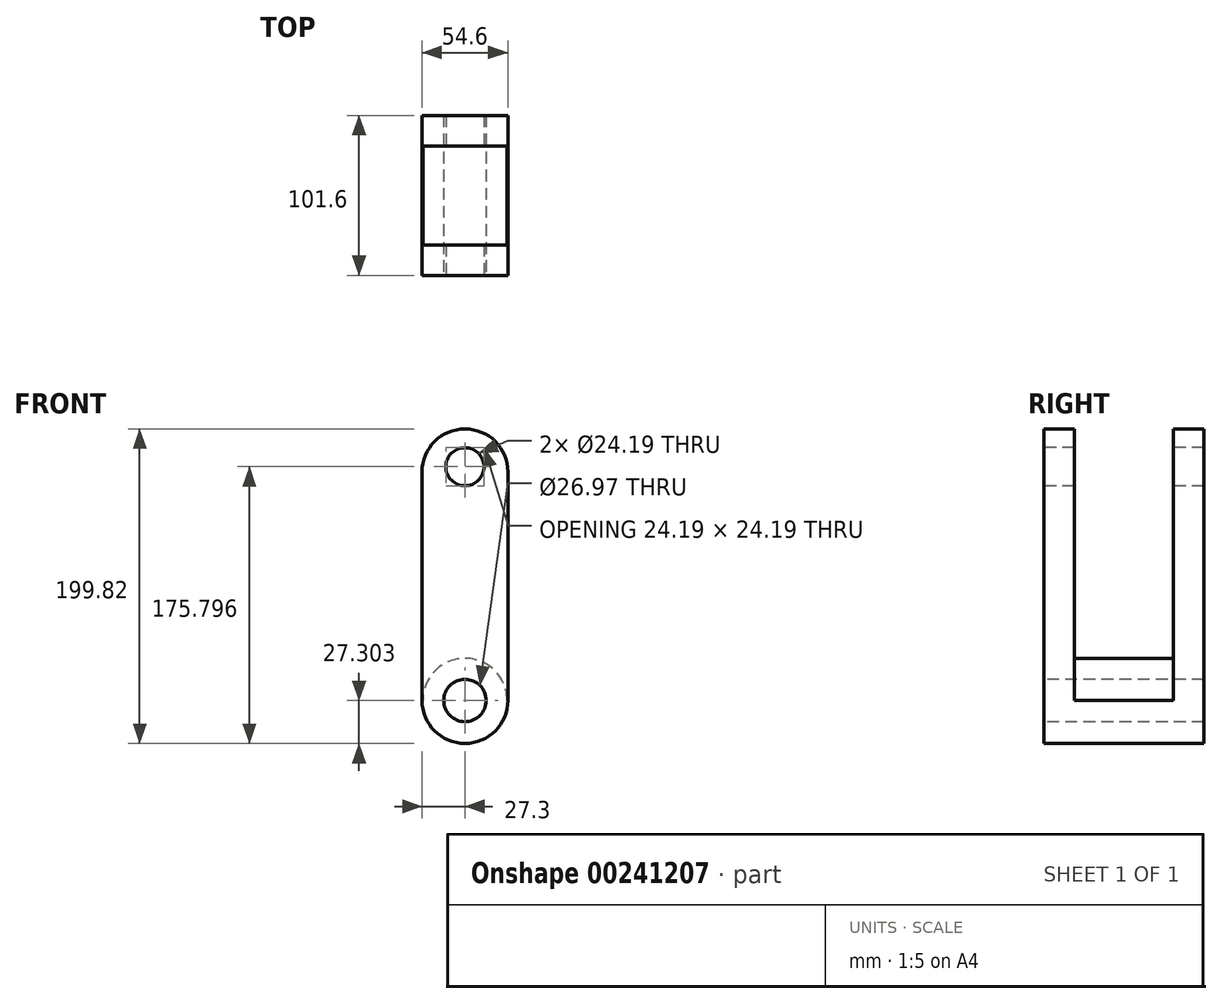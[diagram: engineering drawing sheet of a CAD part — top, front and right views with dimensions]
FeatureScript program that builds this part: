
annotation { "Feature Type Name" : "Feature", "Feature Type Description" : "" }
export const myFeature = defineFeature(function(context is Context, id is Id, definition is map)
    precondition{}
    {
        {
            var Q0;
            Q0=qCreatedBy(makeId("Front.planeOp"),FACE);
            var sketch = newSketch(context, id + "F0", { "sketchPlane" : qUnion([Q0])});
            skLineSegment(sketch, "E0.left", {"start": v(27.3, 72.6) * mm, "end": v(27.3, -72.6) * mm});
            skLineSegment(sketch, "E0.right", {"start": v(-27.3, 72.6) * mm, "end": v(-27.3, -72.6) * mm});
            skPoint(sketch, "E0.middle", {"position": v(0, 0) * mm});
            skArc(sketch, "E1", {"start": v(27.3, 72.6) * mm, "mid": v(0, 99.91) * mm, "end": v(-27.3, 72.6) * mm});
            skArc(sketch, "E2", {"start": v(-27.3, -72.6) * mm, "mid": v(0, -99.91) * mm, "end": v(27.3, -72.6) * mm});
            skSolve(sketch);
        }
        {
            var Q0;
            Q0 = qSketchRegion(id + "F0", true);
            extrude(context, id + "F1", {"entities" : qUnion([Q0]), "oppositeDirection" : true, "depth" : 101.6 * mm});
        }
        {
            var Q0;
            Q0=makeQuery(id+"F1.opExtrude","SWEPT_FACE",FACE,{"disambiguationData":[OSD([sQuery(id+"F0.wireOp",EDGE,"E0.left")])]});
            var sketch = newSketch(context, id + "F2", { "sketchPlane" : qUnion([Q0])});
            skLineSegment(sketch, "E3.bottom", {"start": v(82.2, -72.6) * mm, "end": v(19.4, -72.6) * mm});
            skLineSegment(sketch, "E3.top", {"start": v(82.2, 217.82) * mm, "end": v(19.4, 217.82) * mm});
            skLineSegment(sketch, "E3.left", {"start": v(82.2, -72.6) * mm, "end": v(82.2, 217.82) * mm});
            skLineSegment(sketch, "E3.right", {"start": v(19.4, -72.6) * mm, "end": v(19.4, 217.82) * mm});
            skPoint(sketch, "E3.middle", {"position": v(50.8, 72.6) * mm});
            skSolve(sketch);
        }
        {
            var Q0;
            Q0 = qSketchRegion(id + "F2", true);
            extrude(context, id + "F3", {"entities" : qUnion([Q0]), "operationType" : NewBodyOperationType.REMOVE, "oppositeDirection" : true, "depth" : 76.2 * mm});
        }
        {
            var Q0;
            Q0=qCreatedBy(makeId("Front.planeOp"),FACE);
            var sketch = newSketch(context, id + "F4", { "sketchPlane" : qUnion([Q0])});
            skCircle(sketch, "E4", {"center": v(0, -72.57) * mm, "radius": 26.77 * mm});
            skSolve(sketch);
        }
        {
            var Q0;
            Q0 = qSketchRegion(id + "F4", true);
            extrude(context, id + "F5", {"entities" : qUnion([Q0]), "operationType" : NewBodyOperationType.ADD, "oppositeDirection" : true, "depth" : 101.6 * mm});
        }
        {
            var Q0;
            Q0=makeQuery(id+"F1.opExtrude","CAP_FACE",FACE,{"disambiguationData":[OSD([sQuery(id+"F0.wireOp",EDGE,"E0.left"),sQuery(id+"F0.wireOp",EDGE,"E0.right"),sQuery(id+"F0.wireOp",EDGE,"E1"),sQuery(id+"F0.wireOp",EDGE,"E2")])],"isStart":true});
            var sketch = newSketch(context, id + "F6", { "sketchPlane" : qUnion([Q0])});
            skCircle(sketch, "E5", {"center": v(0, 75.89) * mm, "radius": 12.1 * mm});
            skCircle(sketch, "E6", {"center": v(0, -72.6) * mm, "radius": 13.49 * mm});
            skSolve(sketch);
        }
        {
            var Q0;
            Q0 = qSketchRegion(id + "F6", true);
            extrude(context, id + "F7", {"entities" : qUnion([Q0]), "operationType" : NewBodyOperationType.REMOVE, "oppositeDirection" : true, "depth" : 101.6 * mm});
        }
    });
